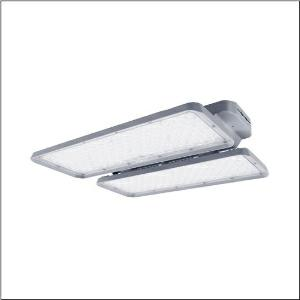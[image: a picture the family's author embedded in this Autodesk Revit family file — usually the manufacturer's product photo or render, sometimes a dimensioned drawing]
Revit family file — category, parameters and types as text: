
# Revit family: highbay_21-l_51hk42db4mca
name_source: partatom
category: Lighting Fixtures
units: mm (PartAtom-declared; Revit-internal decimal feet)

## family parameters
Cut with Voids When Loaded = No
Host = Face
Light Source = No
Part Type = Normal
Room Calculation Point = No
Round Connector Dimension = Use Diameter
Shared = No

## types (1)
- Highbay 21-L (1 x LED, 26500 lm, 147 W, 4000K)
    Apparent Load = 147 VA
    CIE Flux Codes = 75 96 99 100 100
    Color Rendering = 80
    Color Temperature = 4000K
    Default Elevation = 1800 mm
    Description = Highbay 21-L, LED high bay luminaire, primary light control with lens, of PC, light emission: direct distribution, primary light characteristic: symmetric, installation type: suspended mounting, surface-mounted, LED, rated luminous flux: 26.500lm, luminous efficacy: 178lm/W, light colour: 840, colour temperature: 4000K, with terminal, 5-pole, max. 2.5mm², mains connection: 220..240V, AC, 50Hz, rated input power: 147W, housing, of diecast aluminium, coated, grey, length: 471mm, width: 390mm, height: 87mm, protection rating (complete): IP66, insulation class (complete): insulation class I (protective earthing), certification: CE, ENEC, UKCA, protection symbol: D, impact resistance: IK08, permissible operating ambient temperature: -30..+60°C, corresponds to IFS (International Featured Standards) requirements for safety and quality in the food industry, LABS conformity tested according to VDMA 24364:2018-05, packaging unit: 1 piece
    Height = 89 mm
    Lamp = 1 x LED
    Lamp Light Flux = 26500 lm
    Lamp Power = 147 W
    Lamp count = 1
    Length = 471 mm
    Luminous efficacy = 180 lm/W
    Manufacturer = Siteco
    ModVariant = No
    Model = 51HK42DB4MCA
    Mounting Place = Ceiling
    Mounting Type = Pendant
    Number of Poles = 1
    OnlyDefault = Yes
    Power Factor = 1
    Product Name = Highbay 21-L
    Product group = LED high bay luminaire
    ProductGroupID = 903
    Protection Class = Protection class I
    Protection Degree = IP 66
    RLX_Detail_Level = 1
    RLX_Emergency_Light_Flux = 0 lm
    RLX_Emergency_Type = 0
    RLX_Emergency_Type_DB = No
    RlxData = <blob elided: 25969 chars, md5=dbe29c7d>
    Socket = socket
    Standby Power = 0 W
    System Light Flux = 26500 lm
    System Power = 147 W
    Type Comments = Product without accessories
    Type Image = l_1276530.jpg
    URL = http://relux.com
    VarID = ---
    Voltage = 0 V
    Weight = 0.00 kg
    Width = 390 mm

## geometry (parser evidence)
native form markers: Blend x4, Sweep x11
no freeform markers — native parametric forms only
